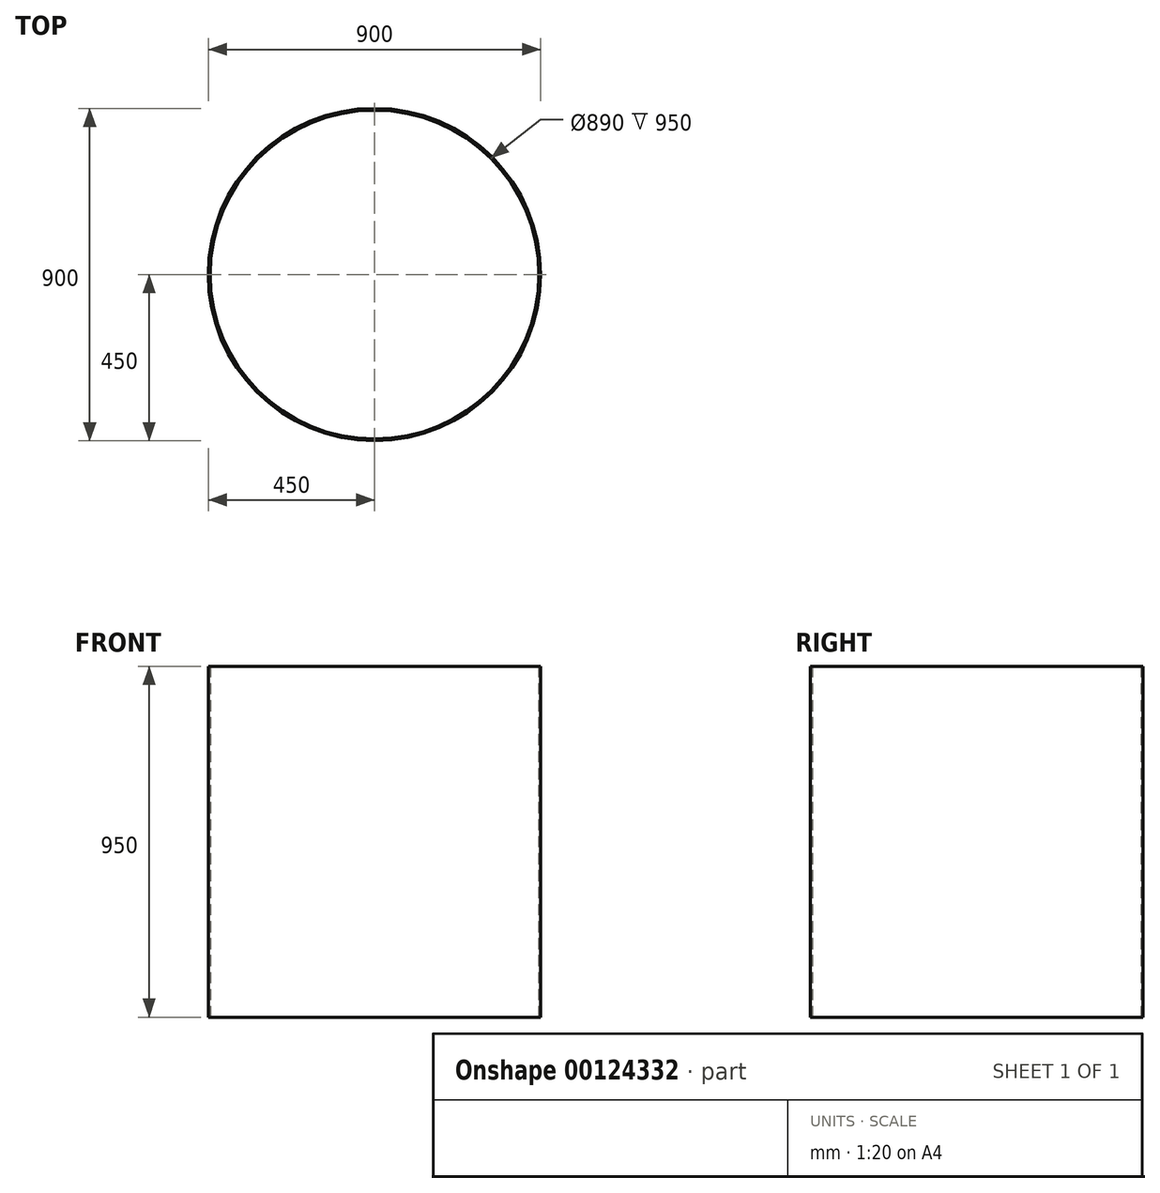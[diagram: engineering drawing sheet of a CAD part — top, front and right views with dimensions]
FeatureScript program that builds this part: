
annotation { "Feature Type Name" : "Feature", "Feature Type Description" : "" }
export const myFeature = defineFeature(function(context is Context, id is Id, definition is map)
    precondition{}
    {
        {
            var Q0;
            Q0=qCreatedBy(makeId("Top.planeOp"),FACE);
            var sketch = newSketch(context, id + "F0", { "sketchPlane" : qUnion([Q0])});
            skCircle(sketch, "E0", {"center": v(0, 0) * mm, "radius": 450 * mm});
            skCircle(sketch, "E1", {"center": v(0, 0) * mm, "radius": 445 * mm});
            skSolve(sketch);
        }
        {
            var Q0;
            Q0=makeQuery(id+"F0.imprint","IMPRINT",FACE,{"disambiguationData":[TD([[makeQuery(id+"F0.imprint","IMPRINT",EDGE,{"derivedFrom":sQuery(id+"F0.wireOp",EDGE,"E0")}),1.0]])]});
            extrude(context, id + "F1", {"entities" : qUnion([Q0]), "depth" : 950 * mm});
        }
    });
